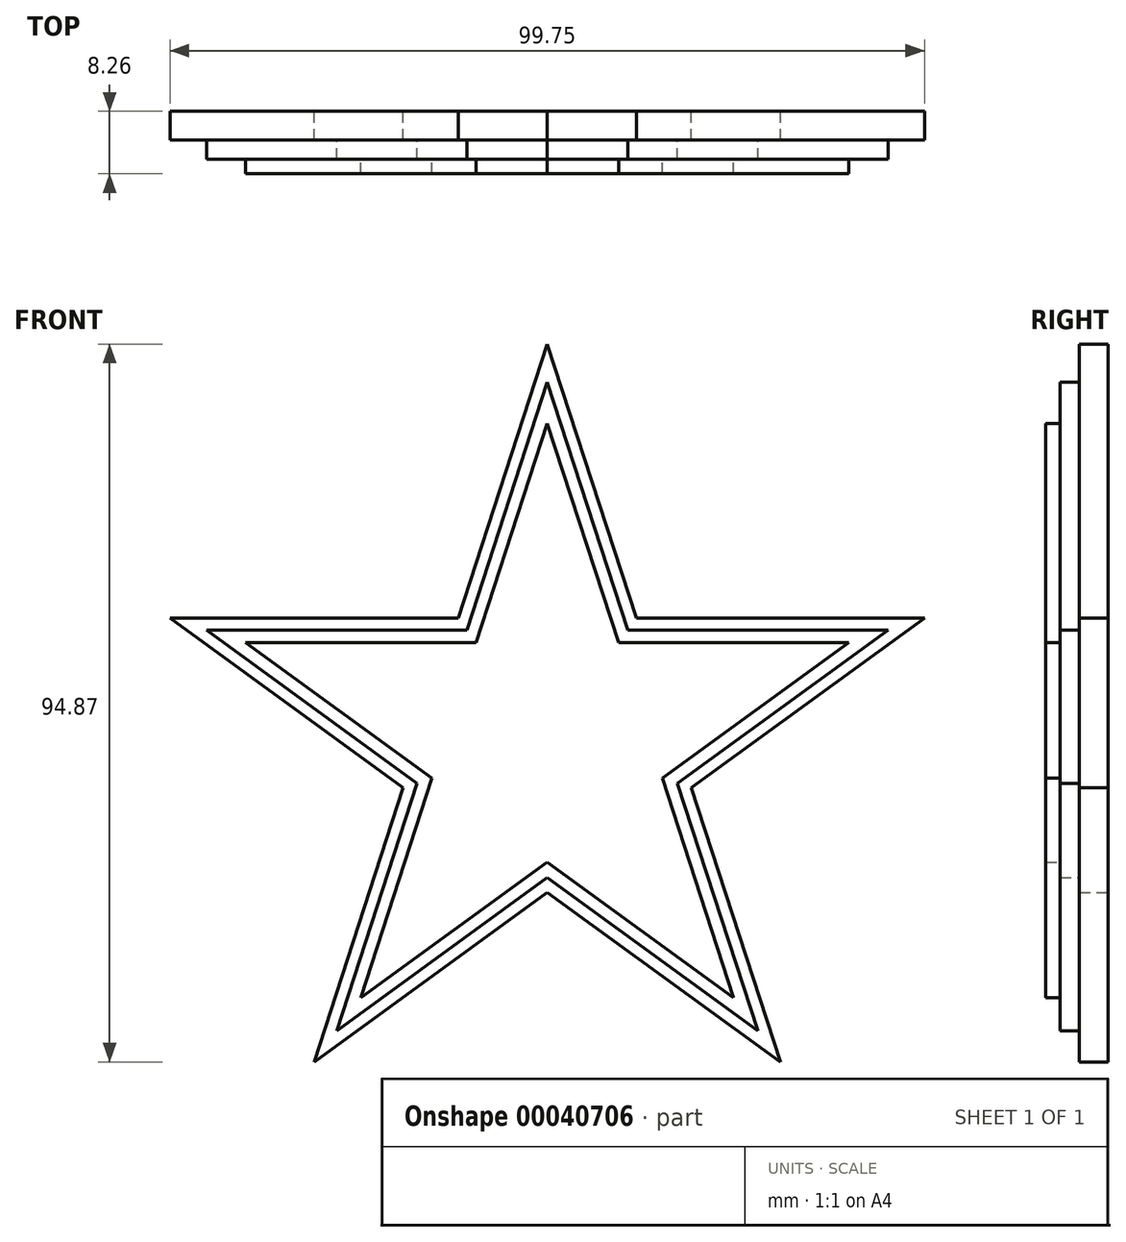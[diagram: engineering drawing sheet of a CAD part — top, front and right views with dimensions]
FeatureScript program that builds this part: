
annotation { "Feature Type Name" : "Feature", "Feature Type Description" : "" }
export const myFeature = defineFeature(function(context is Context, id is Id, definition is map)
    precondition{}
    {
        {
            var Q0;
            Q0=qCreatedBy(makeId("Front.planeOp"),FACE);
            var sketch = newSketch(context, id + "F0", { "sketchPlane" : qUnion([Q0])});
            skLineSegment(sketch, "E0", {"start": v(-255.45, 262.86) * mm, "end": v(-217.35, 262.86) * mm});
            skLineSegment(sketch, "E1", {"start": v(-255.45, 262.86) * mm, "end": v(-267.22, 299.1) * mm});
            skLineSegment(sketch, "E2", {"start": v(-267.22, 299.1) * mm, "end": v(-279, 262.86) * mm});
            skLineSegment(sketch, "E3", {"start": v(-217.35, 262.86) * mm, "end": v(-248.17, 240.47) * mm});
            skLineSegment(sketch, "E4", {"start": v(-279, 262.86) * mm, "end": v(-317.1, 262.86) * mm});
            skLineSegment(sketch, "E5", {"start": v(-317.1, 262.86) * mm, "end": v(-286.27, 240.47) * mm});
            skLineSegment(sketch, "E6", {"start": v(-248.17, 240.47) * mm, "end": v(-236.4, 204.23) * mm});
            skLineSegment(sketch, "E7", {"start": v(-236.4, 204.23) * mm, "end": v(-267.22, 226.63) * mm});
            skLineSegment(sketch, "E8", {"start": v(-286.27, 240.47) * mm, "end": v(-298.05, 204.23) * mm});
            skLineSegment(sketch, "E9", {"start": v(-298.05, 204.23) * mm, "end": v(-267.22, 226.63) * mm});
            skPoint(sketch, "E10.start.orphan", {"position": v(-292.16, 222.35) * mm});
            skSolve(sketch);
        }
        {
            var Q0;
            Q0=makeQuery(id+"F0.imprint","IMPRINT",FACE,{"disambiguationData":[TD([[makeQuery(id+"F0.imprint","IMPRINT",EDGE,{"derivedFrom":sQuery(id+"F0.wireOp",EDGE,"E0")}),-1.0]])]});
            extrude(context, id + "F1", {"entities" : qUnion([Q0]), "depth" : 3.8 * mm});
        }
        {
            var Q0;
            Q0=makeQuery(id+"F1.opExtrude","CAP_FACE",FACE,{"disambiguationData":[OSD([sQuery(id+"F0.wireOp",EDGE,"E0"),sQuery(id+"F0.wireOp",EDGE,"E1"),sQuery(id+"F0.wireOp",EDGE,"E2"),sQuery(id+"F0.wireOp",EDGE,"E3"),sQuery(id+"F0.wireOp",EDGE,"E4"),sQuery(id+"F0.wireOp",EDGE,"E5"),sQuery(id+"F0.wireOp",EDGE,"E6"),sQuery(id+"F0.wireOp",EDGE,"E7"),sQuery(id+"F0.wireOp",EDGE,"E8"),sQuery(id+"F0.wireOp",EDGE,"E9")])],"isStart":false});
            var sketch = newSketch(context, id + "F2", { "sketchPlane" : qUnion([Q0])});
            skLineSegment(sketch, "E11.0", {"start": v(-250.01, 241.07) * mm, "end": v(-222.17, 261.3) * mm});
            skLineSegment(sketch, "E11.1", {"start": v(-239.38, 208.33) * mm, "end": v(-250.01, 241.07) * mm});
            skLineSegment(sketch, "E11.2", {"start": v(-222.17, 261.3) * mm, "end": v(-256.59, 261.3) * mm});
            skLineSegment(sketch, "E11.3", {"start": v(-267.22, 228.56) * mm, "end": v(-239.38, 208.33) * mm});
            skLineSegment(sketch, "E11.4", {"start": v(-295.07, 208.33) * mm, "end": v(-267.22, 228.56) * mm});
            skLineSegment(sketch, "E11.5", {"start": v(-284.43, 241.07) * mm, "end": v(-295.07, 208.33) * mm});
            skLineSegment(sketch, "E11.6", {"start": v(-256.59, 261.3) * mm, "end": v(-267.22, 294.03) * mm});
            skLineSegment(sketch, "E11.7", {"start": v(-267.22, 294.03) * mm, "end": v(-277.86, 261.3) * mm});
            skLineSegment(sketch, "E11.8", {"start": v(-277.86, 261.3) * mm, "end": v(-312.27, 261.3) * mm});
            skLineSegment(sketch, "E11.9", {"start": v(-312.27, 261.3) * mm, "end": v(-284.43, 241.07) * mm});
            skSolve(sketch);
        }
        {
            var Q0;
            Q0=makeQuery(id+"F2.imprint","IMPRINT",FACE,{"disambiguationData":[TD([[makeQuery(id+"F2.imprint","IMPRINT",EDGE,{"derivedFrom":sQuery(id+"F2.wireOp",EDGE,"E11.0")}),1.0]])]});
            extrude(context, id + "F3", {"entities" : qUnion([Q0]), "operationType" : NewBodyOperationType.ADD, "depth" : 2.54 * mm});
        }
        {
            var Q0;
            Q0=makeQuery(id+"F3.opExtrude","CAP_FACE",FACE,{"disambiguationData":[OSD([sQuery(id+"F2.wireOp",EDGE,"E11.0"),sQuery(id+"F2.wireOp",EDGE,"E11.1"),sQuery(id+"F2.wireOp",EDGE,"E11.2"),sQuery(id+"F2.wireOp",EDGE,"E11.3"),sQuery(id+"F2.wireOp",EDGE,"E11.4"),sQuery(id+"F2.wireOp",EDGE,"E11.5"),sQuery(id+"F2.wireOp",EDGE,"E11.6"),sQuery(id+"F2.wireOp",EDGE,"E11.7"),sQuery(id+"F2.wireOp",EDGE,"E11.8"),sQuery(id+"F2.wireOp",EDGE,"E11.9")])],"isStart":false});
            var sketch = newSketch(context, id + "F4", { "sketchPlane" : qUnion([Q0])});
            skLineSegment(sketch, "E12.0", {"start": v(-267.22, 230.64) * mm, "end": v(-242.57, 212.73) * mm});
            skLineSegment(sketch, "E12.1", {"start": v(-291.87, 212.73) * mm, "end": v(-267.22, 230.64) * mm});
            skLineSegment(sketch, "E12.2", {"start": v(-242.57, 212.73) * mm, "end": v(-251.99, 241.7) * mm});
            skLineSegment(sketch, "E12.3", {"start": v(-282.46, 241.7) * mm, "end": v(-291.87, 212.73) * mm});
            skLineSegment(sketch, "E12.4", {"start": v(-307.1, 259.62) * mm, "end": v(-282.46, 241.7) * mm});
            skLineSegment(sketch, "E12.5", {"start": v(-276.64, 259.62) * mm, "end": v(-307.1, 259.62) * mm});
            skLineSegment(sketch, "E12.6", {"start": v(-251.99, 241.7) * mm, "end": v(-227.34, 259.62) * mm});
            skLineSegment(sketch, "E12.7", {"start": v(-227.34, 259.62) * mm, "end": v(-257.8, 259.62) * mm});
            skLineSegment(sketch, "E12.8", {"start": v(-257.8, 259.62) * mm, "end": v(-267.22, 288.6) * mm});
            skLineSegment(sketch, "E12.9", {"start": v(-267.22, 288.6) * mm, "end": v(-276.64, 259.62) * mm});
            skSolve(sketch);
        }
        {
            var Q0;
            Q0=makeQuery(id+"F4.imprint","IMPRINT",FACE,{"disambiguationData":[TD([[makeQuery(id+"F4.imprint","IMPRINT",EDGE,{"derivedFrom":sQuery(id+"F4.wireOp",EDGE,"E12.0")}),1.0]])]});
            extrude(context, id + "F5", {"entities" : qUnion([Q0]), "operationType" : NewBodyOperationType.ADD, "depth" : 1.9 * mm});
        }
    });
